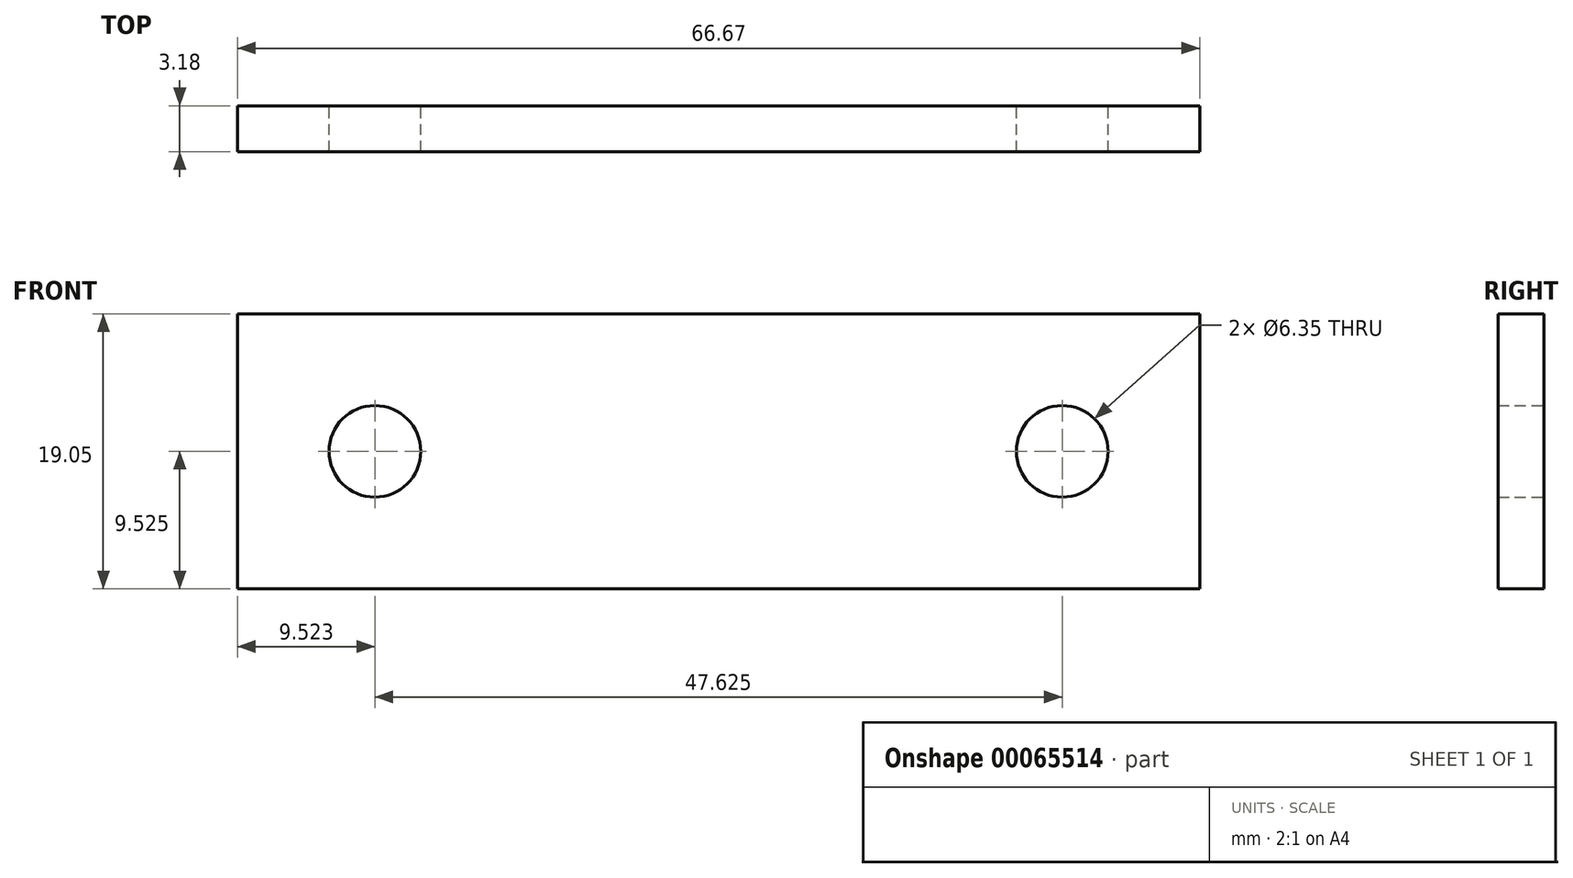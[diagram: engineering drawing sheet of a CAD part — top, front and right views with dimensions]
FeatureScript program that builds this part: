
annotation { "Feature Type Name" : "Feature", "Feature Type Description" : "" }
export const myFeature = defineFeature(function(context is Context, id is Id, definition is map)
    precondition{}
    {
        {
            var Q0;
            Q0=qCreatedBy(makeId("Front.planeOp"),FACE);
            var sketch = newSketch(context, id + "F0", { "sketchPlane" : qUnion([Q0])});
            skLineSegment(sketch, "E0.bottom", {"start": v(-32, 24.91) * mm, "end": v(34.68, 24.91) * mm});
            skLineSegment(sketch, "E0.top", {"start": v(-32, 5.86) * mm, "end": v(34.68, 5.86) * mm});
            skLineSegment(sketch, "E0.left", {"start": v(-32, 24.91) * mm, "end": v(-32, 5.86) * mm});
            skLineSegment(sketch, "E0.right", {"start": v(34.68, 24.91) * mm, "end": v(34.68, 5.86) * mm});
            skLineSegment(sketch, "E1.bottom", {"start": v(-32, 24.91) * mm, "end": v(-22.47, 24.91) * mm});
            skLineSegment(sketch, "E1.top", {"start": v(-32, 15.39) * mm, "end": v(-22.47, 15.39) * mm});
            skLineSegment(sketch, "E1.left", {"start": v(-32, 24.91) * mm, "end": v(-32, 15.39) * mm});
            skLineSegment(sketch, "E1.right", {"start": v(-22.47, 24.91) * mm, "end": v(-22.47, 15.39) * mm});
            skLineSegment(sketch, "E2.bottom", {"start": v(34.68, 5.86) * mm, "end": v(25.16, 5.86) * mm});
            skLineSegment(sketch, "E2.top", {"start": v(34.68, 15.39) * mm, "end": v(25.16, 15.39) * mm});
            skLineSegment(sketch, "E2.left", {"start": v(34.68, 5.86) * mm, "end": v(34.68, 15.39) * mm});
            skLineSegment(sketch, "E2.right", {"start": v(25.16, 5.86) * mm, "end": v(25.16, 15.39) * mm});
            skCircle(sketch, "E3", {"center": v(-22.47, 15.39) * mm, "radius": 3.18 * mm});
            skCircle(sketch, "E4", {"center": v(25.16, 15.39) * mm, "radius": 3.18 * mm});
            skSolve(sketch);
        }
        {
            var Q0;
            Q0 = qSketchRegion(id + "F0", true);
            extrude(context, id + "F1", {"entities" : qUnion([Q0]), "depth" : 3.17 * mm});
        }
    });
